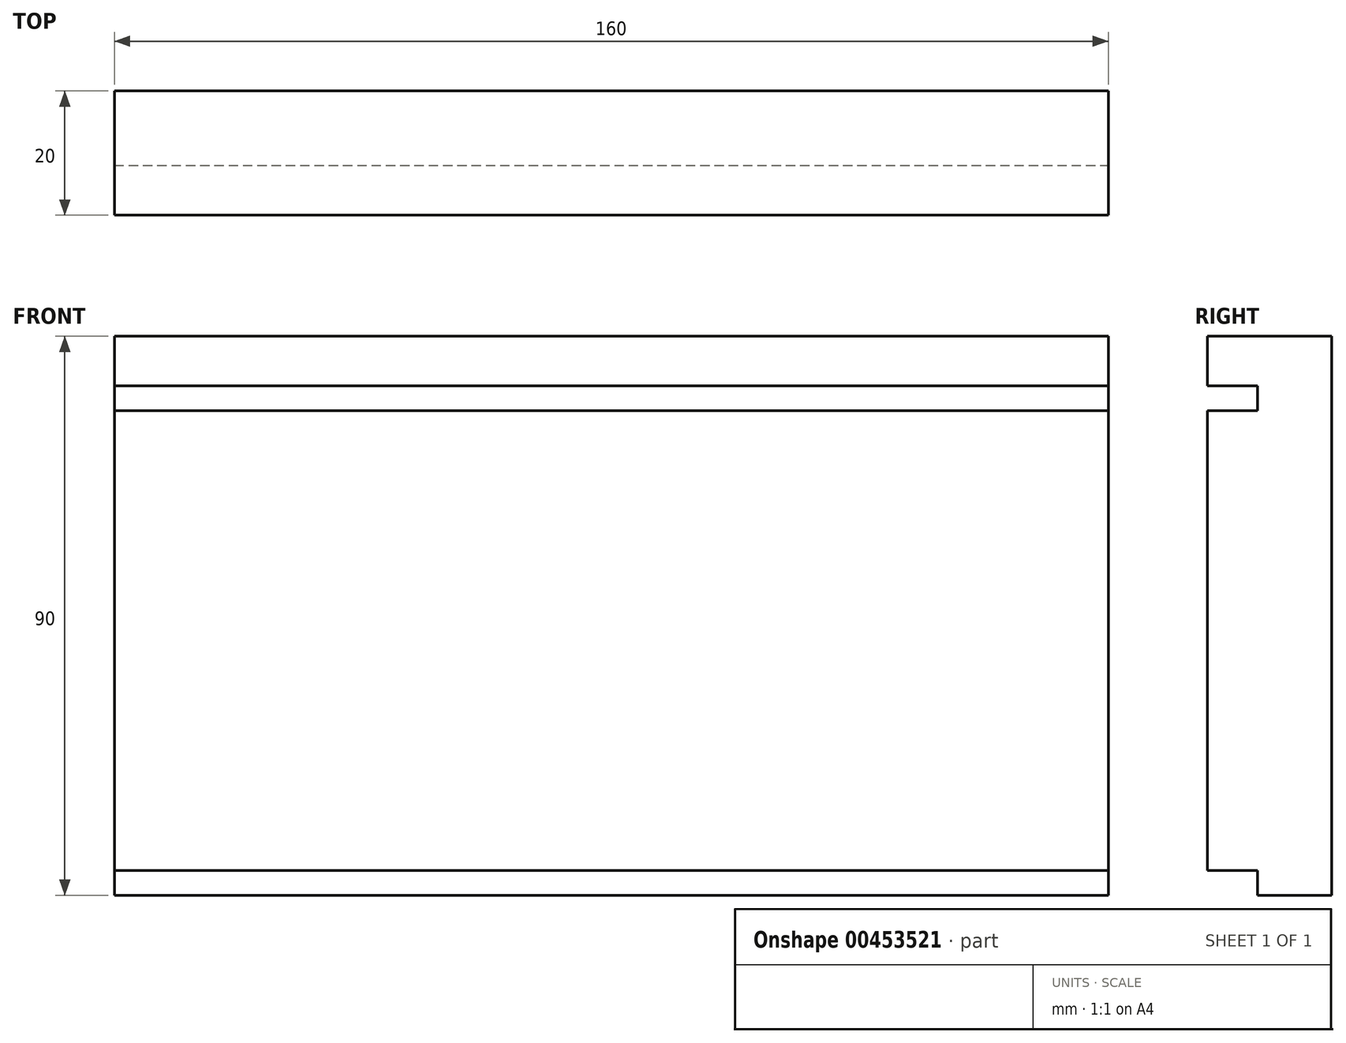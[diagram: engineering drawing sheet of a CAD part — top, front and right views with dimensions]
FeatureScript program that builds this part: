
annotation { "Feature Type Name" : "Feature", "Feature Type Description" : "" }
export const myFeature = defineFeature(function(context is Context, id is Id, definition is map)
    precondition{}
    {
        {
            var Q0;
            Q0=qCreatedBy(makeId("Front.planeOp"),FACE);
            var sketch = newSketch(context, id + "F0", { "sketchPlane" : qUnion([Q0])});
            skLineSegment(sketch, "E0.bottom", {"start": v(-78.98, 3.6) * mm, "end": v(81.02, 3.6) * mm});
            skLineSegment(sketch, "E0.top", {"start": v(-78.98, -86.4) * mm, "end": v(81.02, -86.4) * mm});
            skLineSegment(sketch, "E0.left", {"start": v(-78.98, 3.6) * mm, "end": v(-78.98, -86.4) * mm});
            skLineSegment(sketch, "E0.right", {"start": v(81.02, 3.6) * mm, "end": v(81.02, -86.4) * mm});
            skSolve(sketch);
        }
        {
            var Q0;
            Q0 = qSketchRegion(id + "F0", true);
            extrude(context, id + "F1", {"entities" : qUnion([Q0]), "depth" : 20 * mm});
        }
        {
            var Q0;
            Q0=makeQuery(id+"F1.opExtrude","SWEPT_FACE",FACE,{"disambiguationData":[OSD([sQuery(id+"F0.wireOp",EDGE,"E0.right")])]});
            var sketch = newSketch(context, id + "F2", { "sketchPlane" : qUnion([Q0])});
            skLineSegment(sketch, "E1.bottom", {"start": v(-20, -86.4) * mm, "end": v(-12, -86.4) * mm});
            skLineSegment(sketch, "E1.top", {"start": v(-20, -82.4) * mm, "end": v(-12, -82.4) * mm});
            skLineSegment(sketch, "E1.left", {"start": v(-20, -86.4) * mm, "end": v(-20, -82.4) * mm});
            skLineSegment(sketch, "E1.right", {"start": v(-12, -86.4) * mm, "end": v(-12, -82.4) * mm});
            skLineSegment(sketch, "E2.bottom", {"start": v(-20, -4.4) * mm, "end": v(-12, -4.4) * mm});
            skLineSegment(sketch, "E2.top", {"start": v(-20, -8.4) * mm, "end": v(-12, -8.4) * mm});
            skLineSegment(sketch, "E2.left", {"start": v(-20, -4.4) * mm, "end": v(-20, -8.4) * mm});
            skLineSegment(sketch, "E2.right", {"start": v(-12, -4.4) * mm, "end": v(-12, -8.4) * mm});
            skSolve(sketch);
        }
        {
            var Q0;
            Q0=makeQuery(id+"F2.imprint","IMPRINT",FACE,{"disambiguationData":[TD([[makeQuery(id+"F2.imprint","IMPRINT",EDGE,{"derivedFrom":sQuery(id+"F2.wireOp",EDGE,"E2.bottom")}),-1.0]])]});
            var Q1;
            Q1=makeQuery(id+"F2.imprint","IMPRINT",FACE,{"disambiguationData":[TD([[makeQuery(id+"F2.imprint","IMPRINT",EDGE,{"derivedFrom":sQuery(id+"F2.wireOp",EDGE,"E1.bottom")}),1.0]])]});
            extrude(context, id + "F3", {"entities" : qUnion([Q0, Q1]), "operationType" : NewBodyOperationType.REMOVE, "oppositeDirection" : true, "depth" : 160 * mm});
        }
    });
